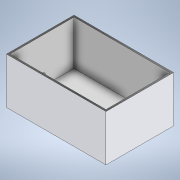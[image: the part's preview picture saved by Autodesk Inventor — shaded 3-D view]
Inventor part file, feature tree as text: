
AUTODESK INVENTOR PART (.ipt)
format: ipt  version: 2020 (Build 240168000, 168)  size: 129,536 bytes
history: native  units: mm
features: extrude x4, sketch x4, other x2, plane x2, projected_geometry x1
ambient origin geometry x8: Origin, YZ Plane, XZ Plane, XY Plane, X Axis, Y Axis, Z Axis, Center Point
bodies: Body1 (feature_tree)
feature tree (13):
  other  "Sólido1"
  extrude  "Extrusión1"  Depth=190.0mm
  other  "Eje de trabajo1"
  extrude  "Extrusión2"  Depth=140.0mm
  extrude  "Extrusión3"  Depth=270.0mm
  extrude  "Extrusión4"  Depth=180.0mm
  sketch  "Boceto1"  dims[d0=280.0mm d1=190.0mm]
  plane  "Plano de trabajo1"
  plane  "Plano de trabajo2"
  sketch  "Boceto3"  dims[d2=95.0mm d3=140.0mm]
  projected_geometry  "Contorno proyectado1"
  sketch  "Boceto4"  dims[d4=130.0mm d5=0.0mm d7=270.0mm]
  sketch  "Boceto6"  dims[d8=135.0mm d9=180.0mm d10=90.0mm d11=125.0mm d12=0.0mm d13=20.0mm d14=5.0mm d15=0.0mm d16=5.0mm d17=0.0mm]
